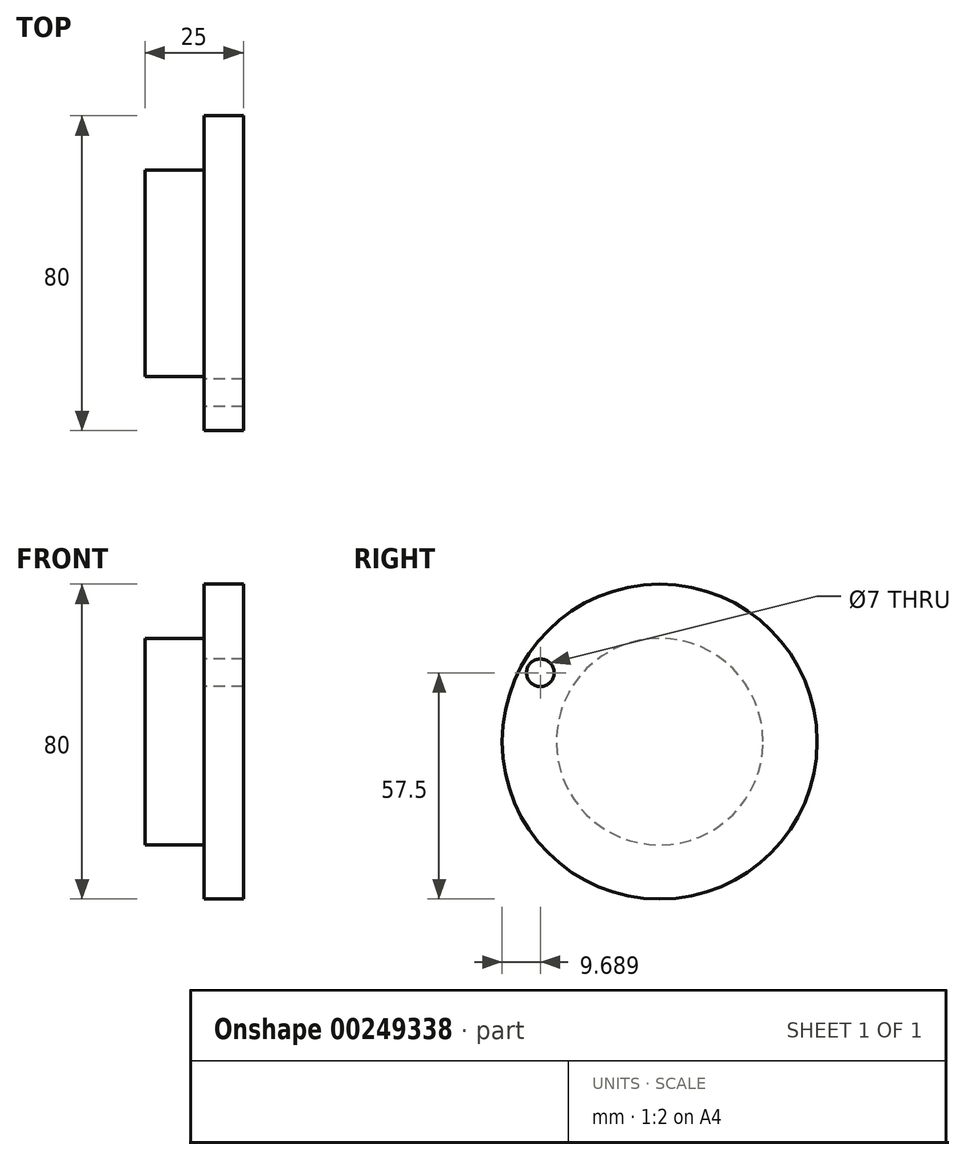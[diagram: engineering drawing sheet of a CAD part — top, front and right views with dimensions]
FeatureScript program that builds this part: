
annotation { "Feature Type Name" : "Feature", "Feature Type Description" : "" }
export const myFeature = defineFeature(function(context is Context, id is Id, definition is map)
    precondition{}
    {
        {
            var Q0;
            Q0=qCreatedBy(makeId("Front.planeOp"),FACE);
            var sketch = newSketch(context, id + "F0", { "sketchPlane" : qUnion([Q0])});
            skLineSegment(sketch, "E0", {"start": v(0, 0) * mm, "end": v(-57.54, 0) * mm, "construction": true});
            skLineSegment(sketch, "E1", {"start": v(0, 26.25) * mm, "end": v(0, 0) * mm});
            skLineSegment(sketch, "E2", {"start": v(15, 0) * mm, "end": v(15, 26.25) * mm});
            skLineSegment(sketch, "E3", {"start": v(0, 26.25) * mm, "end": v(15, 26.25) * mm});
            skLineSegment(sketch, "E4", {"start": v(0, 0) * mm, "end": v(15, 0) * mm});
            skSolve(sketch);
        }
        {
            var Q0;
            Q0=makeQuery(id+"F0.imprint","IMPRINT",FACE,{"disambiguationData":[TD([[makeQuery(id+"F0.imprint","IMPRINT",EDGE,{"derivedFrom":sQuery(id+"F0.wireOp",EDGE,"E1")}),1.0]])]});
            var Q1;
            Q1=sQuery(id+"F0.wireOp",EDGE,"E0");
            revolve(context, id + "F1", {"entities" : qUnion([Q0]), "axis" : qUnion([Q1]), "revolveType" : RevolveType.FULL});
        }
        {
            var Q0;
            Q0=makeQuery(id+"F1.opRevolve","SWEPT_FACE",FACE,{"disambiguationData":[OSD([sQuery(id+"F0.wireOp",EDGE,"E2")])]});
            var sketch = newSketch(context, id + "F2", { "sketchPlane" : qUnion([Q0])});
            skCircle(sketch, "E5", {"center": v(0, 0) * mm, "radius": 40 * mm});
            skSolve(sketch);
        }
        {
            var Q0;
            Q0=makeQuery(id+"F2.imprint","IMPRINT",FACE,{"disambiguationData":[TD([[makeQuery(id+"F2.imprint","IMPRINT",EDGE,{"derivedFrom":makeQuery(id+"F1.opRevolve","SWEPT_EDGE",EDGE,{"disambiguationData":[OSD([sQuery(id+"F0.wireOp",EDGE,"E2"),sQuery(id+"F0.wireOp",EDGE,"E3")])]})}),1.0]])]});
            var Q1;
            Q1=makeQuery(id+"F2.imprint","IMPRINT",FACE,{"disambiguationData":[TD([[makeQuery(id+"F2.imprint","IMPRINT",EDGE,{"derivedFrom":sQuery(id+"F2.wireOp",EDGE,"E5")}),1.0]])]});
            extrude(context, id + "F3", {"entities" : qUnion([Q0, Q1]), "operationType" : NewBodyOperationType.ADD, "depth" : 10 * mm, "offsetDistance" : 25 * mm});
        }
        {
            var Q0;
            Q0=makeQuery(id+"F1.opRevolve","SWEPT_FACE",FACE,{"disambiguationData":[OSD([sQuery(id+"F0.wireOp",EDGE,"E1")])]});
            var sketch = newSketch(context, id + "F4", { "sketchPlane" : qUnion([Q0])});
            skLineSegment(sketch, "E6", {"start": v(0, 0) * mm, "end": v(30.31, 17.5) * mm, "construction": true});
            skCircle(sketch, "E7", {"center": v(30.31, 17.5) * mm, "radius": 3.5 * mm});
            skSolve(sketch);
        }
        {
            var Q0;
            Q0=makeQuery(id+"F4.imprint","IMPRINT",FACE,{"disambiguationData":[TD([[makeQuery(id+"F4.imprint","IMPRINT",EDGE,{"derivedFrom":sQuery(id+"F4.wireOp",EDGE,"E7")}),1.0]])]});
            extrude(context, id + "F5", {"entities" : qUnion([Q0]), "operationType" : NewBodyOperationType.REMOVE, "endBound" : BoundingType.THROUGH_ALL, "oppositeDirection" : true, "depth" : 25 * mm, "offsetDistance" : 25 * mm});
        }
    });
